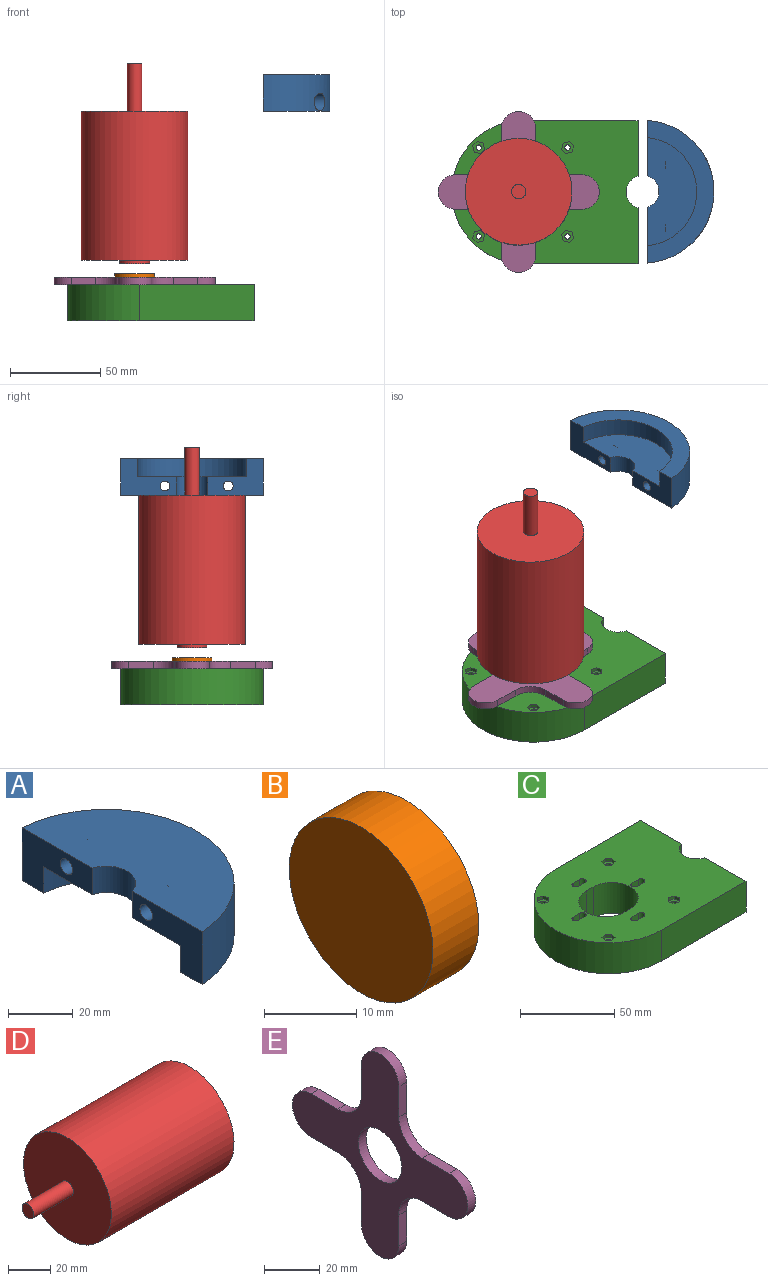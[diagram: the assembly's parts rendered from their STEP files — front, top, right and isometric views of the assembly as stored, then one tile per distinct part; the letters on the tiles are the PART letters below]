
ASSEMBLY  parts=5 mates=8
PART A: 14 faces, bbox 37x78.8x20 mm
  f0: cylinder r=39.5mm len=78.84mm, axis (0,0,-1), area 2213.9mm2, adj f3,f5,f6,f7,f10,f12
  f1: cylinder r=30mm len=59.79mm, axis (0,0,-1), area 892.4mm2, adj f2,f5,f6,f7
  f2: plane 59.79x27.5mm, normal (0,0,-1), area 1178.7mm2, adj f1,f4,f6,f7
  f3: plane 78.84x37mm, normal (0,0,1), area 2168.3mm2, adj f0,f4,f6,f7
  f4: cylinder r=9.1mm len=17.5mm, axis (0,0,1), area 235.2mm2, adj f2,f3,f6,f7
  f5: plane 78.84x37mm, normal (0,0,-1), area 989.6mm2, adj f0,f1,f6,f7
  f6: plane 30.67x20mm, normal (-1,0,0), area 378.2mm2, adj f0,f1,f2,f3,f4,f5,f9
  f7: plane 30.67x20mm, normal (-1,0,0), area 378.2mm2, adj f0,f1,f2,f3,f4,f5,f8
  f8: cylinder r=2.75mm len=10mm, axis (-1,0,0), area 172.8mm2, adj f7,f13
  f9: cylinder r=2.75mm len=10mm, axis (-1,0,0), area 172.8mm2, adj f6,f11
  f10: cylinder r=4.88mm len=25.7mm, axis (-1,0,0), area 731.3mm2, adj f0,f11
  f11: plane 9.75x9.75mm, normal (1,0,0), area 50.9mm2, adj f9,f10
  f12: cylinder r=4.88mm len=23.99mm, axis (-1,0,0), area 653.2mm2, adj f0,f13
  f13: plane 9.75x9.75mm, normal (1,0,0), area 50.9mm2, adj f8,f12
PART B: 3 faces, bbox 7x22x22 mm
  f0: cylinder r=11mm len=22mm, axis (-1,0,0), area 483.8mm2, adj f1,f2
  f1: plane 22x22mm, normal (1,0,0), area 380.1mm2, adj f0
  f2: plane 22x22mm, normal (-1,0,0), area 380.1mm2, adj f0
PART C: 60 faces, bbox 103x79x20 mm
  f0: plane 103x79mm, normal (0,0,-1), area 6467.9mm2, adj f2,f3,f4,f5,f6,f7,f8,f9
  f1: plane 103x79mm, normal (0,0,1), area 6371.5mm2, adj f2,f3,f4,f5,f6,f7,f8,f9
  f2: plane 63.5x20mm, normal (0,1,0), area 1270mm2, adj f0,f1,f3,f58
  f3: cylinder r=39.5mm len=79mm, axis (0,0,-1), area 2481.9mm2, adj f0,f1,f2,f4
  f4: plane 63.5x20mm, normal (0,-1,0), area 1270mm2, adj f0,f1,f3,f59
  f5: plane 20x5mm, normal (0,-1,0), area 100mm2, adj f0,f1,f6,f8
  f6: cylinder r=2mm len=20mm, axis (0,0,1), area 125.7mm2, adj f0,f1,f5,f7
  f7: plane 20x5mm, normal (0,1,0), area 100mm2, adj f0,f1,f6,f8
  f8: cylinder r=2mm len=20mm, axis (0,0,1), area 125.7mm2, adj f0,f1,f5,f7
  f9: plane 20x5mm, normal (0,-1,0), area 100mm2, adj f0,f1,f10,f12
  f10: cylinder r=2mm len=20mm, axis (0,0,1), area 125.7mm2, adj f0,f1,f9,f11
  f11: plane 20x5mm, normal (0,1,0), area 100mm2, adj f0,f1,f10,f12
  f12: cylinder r=2mm len=20mm, axis (0,0,1), area 125.7mm2, adj f0,f1,f9,f11
  f13: plane 20x5mm, normal (0,-1,0), area 100mm2, adj f0,f1,f14,f16
  f14: cylinder r=2mm len=20mm, axis (0,0,1), area 125.7mm2, adj f0,f1,f13,f15
  f15: plane 20x5mm, normal (0,1,0), area 100mm2, adj f0,f1,f14,f16
  f16: cylinder r=2mm len=20mm, axis (0,0,1), area 125.7mm2, adj f0,f1,f13,f15
  f17: cylinder r=2mm len=20mm, axis (0,0,1), area 125.7mm2, adj f0,f1,f18,f20
  f18: plane 20x5mm, normal (0,1,0), area 100mm2, adj f0,f1,f17,f19
  f19: cylinder r=2mm len=20mm, axis (0,0,1), area 125.7mm2, adj f0,f1,f18,f20
  f20: plane 20x5mm, normal (0,-1,0), area 100mm2, adj f0,f1,f17,f19
  f21: plane 20x5mm, normal (0,-1,0), area 100mm2, adj f0,f1,f22,f24
  f22: cylinder r=14mm len=28mm, axis (0,0,1), area 879.6mm2, adj f0,f1,f21,f23
  f23: plane 20x5mm, normal (0,1,0), area 100mm2, adj f0,f1,f22,f24
  f24: cylinder r=14mm len=28mm, axis (0,0,1), area 879.6mm2, adj f0,f1,f21,f23
  f25: plane 2.45x2.45mm, normal (-0.71,-0.71,0), area 6.9mm2, adj f1,f26,f30,f31
  f26: plane 3.35x2mm, normal (0.26,-0.97,0), area 6.9mm2, adj f1,f25,f27,f31
  f27: plane 3.35x2mm, normal (0.97,-0.26,0), area 6.9mm2, adj f1,f26,f28,f31
  f28: plane 2.45x2.45mm, normal (0.71,0.71,0), area 6.9mm2, adj f1,f27,f29,f31
  f29: plane 3.35x2mm, normal (-0.26,0.97,0), area 6.9mm2, adj f1,f28,f30,f31
  f30: plane 3.35x2mm, normal (-0.97,0.26,0), area 6.9mm2, adj f1,f25,f29,f31
  f31: plane 6.69x6.69mm, normal (0,0,1), area 24.1mm2, adj f25,f26,f27,f28,f29,f30,f32
  f32: cylinder r=1.5mm len=18mm, axis (0,0,1), area 169.6mm2, adj f0,f31
  f33: plane 2.45x2.45mm, normal (0.71,-0.71,0), area 6.9mm2, adj f1,f34,f38,f39
  f34: plane 3.35x2mm, normal (0.97,0.26,0), area 6.9mm2, adj f1,f33,f35,f39
  f35: plane 3.35x2mm, normal (0.26,0.97,0), area 6.9mm2, adj f1,f34,f36,f39
  f36: plane 2.45x2.45mm, normal (-0.71,0.71,0), area 6.9mm2, adj f1,f35,f37,f39
  f37: plane 3.35x2mm, normal (-0.97,-0.26,0), area 6.9mm2, adj f1,f36,f38,f39
  f38: plane 3.35x2mm, normal (-0.26,-0.97,0), area 6.9mm2, adj f1,f33,f37,f39
  f39: plane 6.69x6.69mm, normal (0,0,1), area 24.1mm2, adj f33,f34,f35,f36,f37,f38,f40
  f40: cylinder r=1.5mm len=18mm, axis (0,0,1), area 169.6mm2, adj f0,f39
  f41: plane 2.45x2.45mm, normal (0.71,0.71,0), area 6.9mm2, adj f1,f42,f46,f47
  f42: plane 3.35x2mm, normal (-0.26,0.97,0), area 6.9mm2, adj f1,f41,f43,f47
  f43: plane 3.35x2mm, normal (-0.97,0.26,0), area 6.9mm2, adj f1,f42,f44,f47
  f44: plane 2.45x2.45mm, normal (-0.71,-0.71,0), area 6.9mm2, adj f1,f43,f45,f47
  f45: plane 3.35x2mm, normal (0.26,-0.97,0), area 6.9mm2, adj f1,f44,f46,f47
  f46: plane 3.35x2mm, normal (0.97,-0.26,0), area 6.9mm2, adj f1,f41,f45,f47
  f47: plane 6.69x6.69mm, normal (0,0,1), area 24.1mm2, adj f41,f42,f43,f44,f45,f46,f48
  f48: cylinder r=1.5mm len=18mm, axis (0,0,1), area 169.6mm2, adj f0,f47
  f49: plane 2.45x2.45mm, normal (-0.71,0.71,0), area 6.9mm2, adj f1,f50,f54,f55
  f50: plane 3.35x2mm, normal (-0.97,-0.26,0), area 6.9mm2, adj f1,f49,f51,f55
  f51: plane 3.35x2mm, normal (-0.26,-0.97,0), area 6.9mm2, adj f1,f50,f52,f55
  f52: plane 2.45x2.45mm, normal (0.71,-0.71,0), area 6.9mm2, adj f1,f51,f53,f55
  f53: plane 3.35x2mm, normal (0.97,0.26,0), area 6.9mm2, adj f1,f52,f54,f55
  f54: plane 3.35x2mm, normal (0.26,0.97,0), area 6.9mm2, adj f1,f49,f53,f55
  f55: plane 6.69x6.69mm, normal (0,0,1), area 24.1mm2, adj f49,f50,f51,f52,f53,f54,f56
  f56: cylinder r=1.5mm len=18mm, axis (0,0,1), area 169.6mm2, adj f0,f55
  f57: cylinder r=9.1mm len=20mm, axis (0,0,1), area 470.5mm2, adj f0,f1,f58,f59
  f58: plane 30.75x20mm, normal (1,0,0), area 615mm2, adj f0,f1,f2,f57
  f59: plane 30.75x20mm, normal (1,0,0), area 615mm2, adj f0,f1,f4,f57
PART D: 7 faces, bbox 110.8x59x59 mm
  f0: cylinder r=29.5mm len=82.4mm, axis (-1,0,0), area 15273.2mm2, adj f1,f2
  f1: plane 59x59mm, normal (1,0,0), area 2520.1mm2, adj f0,f5
  f2: plane 59x59mm, normal (-1,0,0), area 2683.7mm2, adj f0,f3
  f3: cylinder r=4mm len=26.5mm, axis (1,0,0), area 666mm2, adj f2,f4
  f4: plane 8x8mm, normal (-1,0,0), area 50.3mm2, adj f3
  f5: cylinder r=8.25mm len=16.5mm, axis (-1,0,0), area 98.5mm2, adj f1,f6
  f6: plane 16.5x16.5mm, normal (1,0,0), area 213.8mm2, adj f5
PART E: 19 faces, bbox 4x89x89 mm
  f0: cylinder r=9.5mm len=19mm, axis (1,0,0), area 119.4mm2, adj f1,f12,f13,f14
  f1: plane 13.5x4mm, normal (0,-1,0), area 54mm2, adj f0,f13,f14,f15
  f2: plane 13.5x4mm, normal (0,0,1), area 54mm2, adj f3,f13,f14,f15
  f3: cylinder r=9.5mm len=19mm, axis (1,0,0), area 119.4mm2, adj f2,f4,f13,f14
  f4: plane 13.5x4mm, normal (0,0,-1), area 54mm2, adj f3,f13,f14,f16
  f5: plane 13.5x4mm, normal (0,-1,0), area 54mm2, adj f6,f13,f14,f16
  f6: cylinder r=9.5mm len=19mm, axis (1,0,0), area 119.4mm2, adj f5,f7,f13,f14
  f7: plane 13.5x4mm, normal (0,1,0), area 54mm2, adj f6,f13,f14,f17
  f8: plane 13.5x4mm, normal (0,0,-1), area 54mm2, adj f9,f13,f14,f17
  f9: cylinder r=9.5mm len=19mm, axis (1,0,0), area 119.4mm2, adj f8,f10,f13,f14
  f10: plane 13.5x4mm, normal (0,0,1), area 54mm2, adj f9,f13,f14,f18
  f11: cylinder r=11mm len=22mm, axis (1,0,0), area 276.5mm2, adj f13,f14
  f12: plane 13.5x4mm, normal (0,1,0), area 54mm2, adj f0,f13,f14,f18
  f13: plane 89x89mm, normal (-1,0,0), area 2609.5mm2, adj f0,f1,f2,f3,f4,f5,f6,f7
  f14: plane 89x89mm, normal (1,0,0), area 2609.5mm2, adj f0,f1,f2,f3,f4,f5,f6,f7
  f15: cylinder r=12mm len=12mm, axis (1,0,0), area 75.4mm2, adj f1,f2,f13,f14
  f16: cylinder r=12mm len=12mm, axis (-1,0,0), area 75.4mm2, adj f4,f5,f13,f14
  f17: cylinder r=12mm len=12mm, axis (1,0,0), area 75.4mm2, adj f7,f8,f13,f14
  f18: cylinder r=12mm len=12mm, axis (-1,0,0), area 75.4mm2, adj f10,f12,f13,f14
PLACE A rot(axis=(-1,0,0),180deg) t=(-45.37,27.44,190.51)mm
PLACE B rot(axis=(0.6,-0.53,0.6),124.1deg) t=(-113.87,27.44,73.51)mm
PLACE C t=(-45.37,27.44,54.51)mm fixed
PLACE D rot(axis=(0,1,0),90deg) t=(-113.87,27.44,170.51)mm
PLACE E rot(axis=(0,1,0),90deg) t=(-113.87,27.44,74.51)mm
MATE planar A.f3 <-> B.f0  axis (0,0,-1) through (-83.48,1.99,170.51)mm
MATE cylindrical A.f0 <-> C.f57  axis (0,0,1) through (-45.37,27.44,180.51)mm
MATE fastened A.f4 <-> C.f57  axis (0,0,-1) through (-45.37,27.44,170.51)mm
MATE cylindrical C.f22 <-> D.f0  axis (0,0,-1) through (-113.87,27.44,54.51)mm
MATE planar D.f0 <-> A.f3  axis (0,0,1) through (-113.87,27.44,170.51)mm
MATE planar E.f3 <-> C.f1  axis (0,0,-1) through (-113.87,-7.56,74.51)mm
MATE cylindrical B.f0 <-> D.f0  axis (0,0,1) through (-113.87,27.44,80.51)mm
MATE cylindrical E.f11 <-> D.f0  axis (0,0,-1) through (-113.87,27.44,76.51)mm
